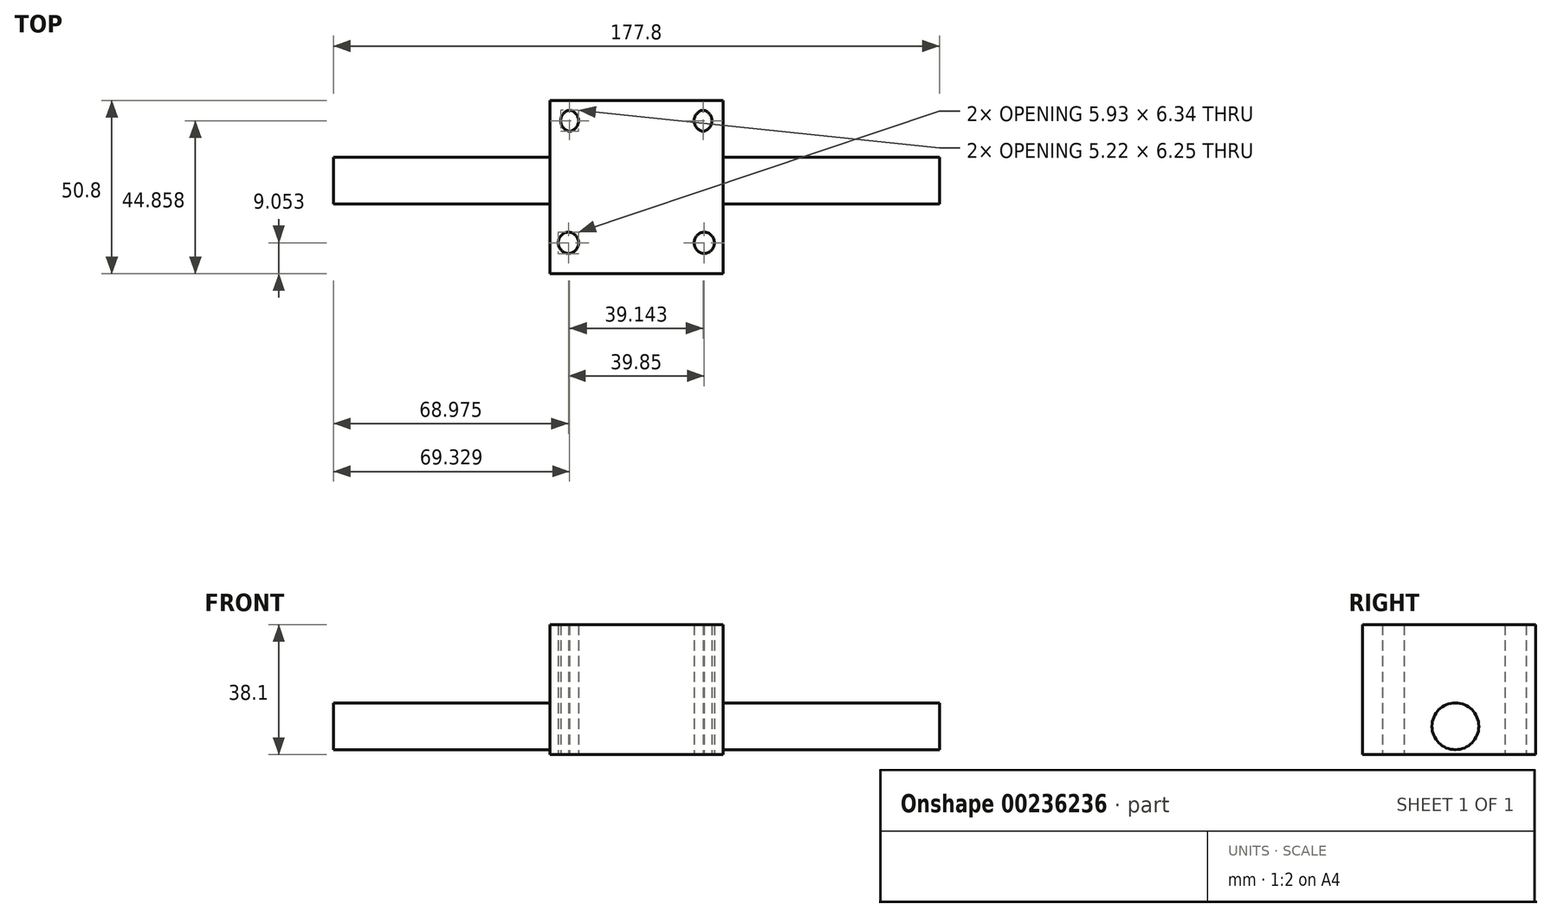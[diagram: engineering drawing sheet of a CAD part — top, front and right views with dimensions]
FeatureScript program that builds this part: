
annotation { "Feature Type Name" : "Feature", "Feature Type Description" : "" }
export const myFeature = defineFeature(function(context is Context, id is Id, definition is map)
    precondition{}
    {
        {
            var Q0;
            Q0=qCreatedBy(makeId("Top.planeOp"),FACE);
            var sketch = newSketch(context, id + "F0", { "sketchPlane" : qUnion([Q0])});
            skLineSegment(sketch, "E0.bottom", {"start": v(25.4, -25.4) * mm, "end": v(-25.4, -25.4) * mm});
            skLineSegment(sketch, "E0.top", {"start": v(25.4, 25.4) * mm, "end": v(-25.4, 25.4) * mm});
            skLineSegment(sketch, "E0.left", {"start": v(25.4, -25.4) * mm, "end": v(25.4, 25.4) * mm});
            skLineSegment(sketch, "E0.right", {"start": v(-25.4, -25.4) * mm, "end": v(-25.4, 25.4) * mm});
            skPoint(sketch, "E0.middle", {"position": v(0, 0) * mm});
            skCircle(sketch, "E1", {"center": v(-20.13, 19.46) * mm, "radius": 3.18 * mm});
            skCircle(sketch, "E2", {"center": v(19, 19.46) * mm, "radius": 3.18 * mm});
            skCircle(sketch, "E3", {"center": v(-20.13, -16.35) * mm, "radius": 3.18 * mm});
            skCircle(sketch, "E4", {"center": v(19.72, -16.35) * mm, "radius": 3.18 * mm});
            skSolve(sketch);
        }
        {
            var Q0;
            Q0 = qSketchRegion(id + "F0", true);
            extrude(context, id + "F1", {"entities" : qUnion([Q0]), "endBound" : BoundingType.SYMMETRIC, "depth" : 38.1 * mm});
        }
        {
            var Q0;
            Q0=makeQuery(id+"F1.opExtrude","SWEPT_FACE",FACE,{"disambiguationData":[OSD([sQuery(id+"F0.wireOp",EDGE,"E0.right")])]});
            var sketch = newSketch(context, id + "F2", { "sketchPlane" : qUnion([Q0])});
            skCircle(sketch, "E5", {"center": v(-1.86, -10.75) * mm, "radius": 6.87 * mm});
            skSolve(sketch);
        }
        {
            var Q0;
            Q0 = qSketchRegion(id + "F2", true);
            extrude(context, id + "F3", {"entities" : qUnion([Q0]), "operationType" : NewBodyOperationType.ADD, "depth" : 63.5 * mm});
        }
        {
            var Q0;
            Q0=makeQuery(id+"F1.opExtrude","SWEPT_BODY",BODY,{"disambiguationData":[OSD([sQuery(id+"F0.wireOp",EDGE,"E0.bottom"),sQuery(id+"F0.wireOp",EDGE,"E0.top"),sQuery(id+"F0.wireOp",EDGE,"E0.left"),sQuery(id+"F0.wireOp",EDGE,"E0.right"),sQuery(id+"F0.wireOp",EDGE,"E1"),sQuery(id+"F0.wireOp",EDGE,"E2"),sQuery(id+"F0.wireOp",EDGE,"E3"),sQuery(id+"F0.wireOp",EDGE,"E4")])]});
            var Q1;
            Q1=qCreatedBy(makeId("Right.planeOp"),FACE);
            mirror(context, id + "F4", {"operationType" : NewBodyOperationType.ADD, "entities" : qUnion([Q0]), "mirrorPlane" : qUnion([Q1])});
        }
    });
